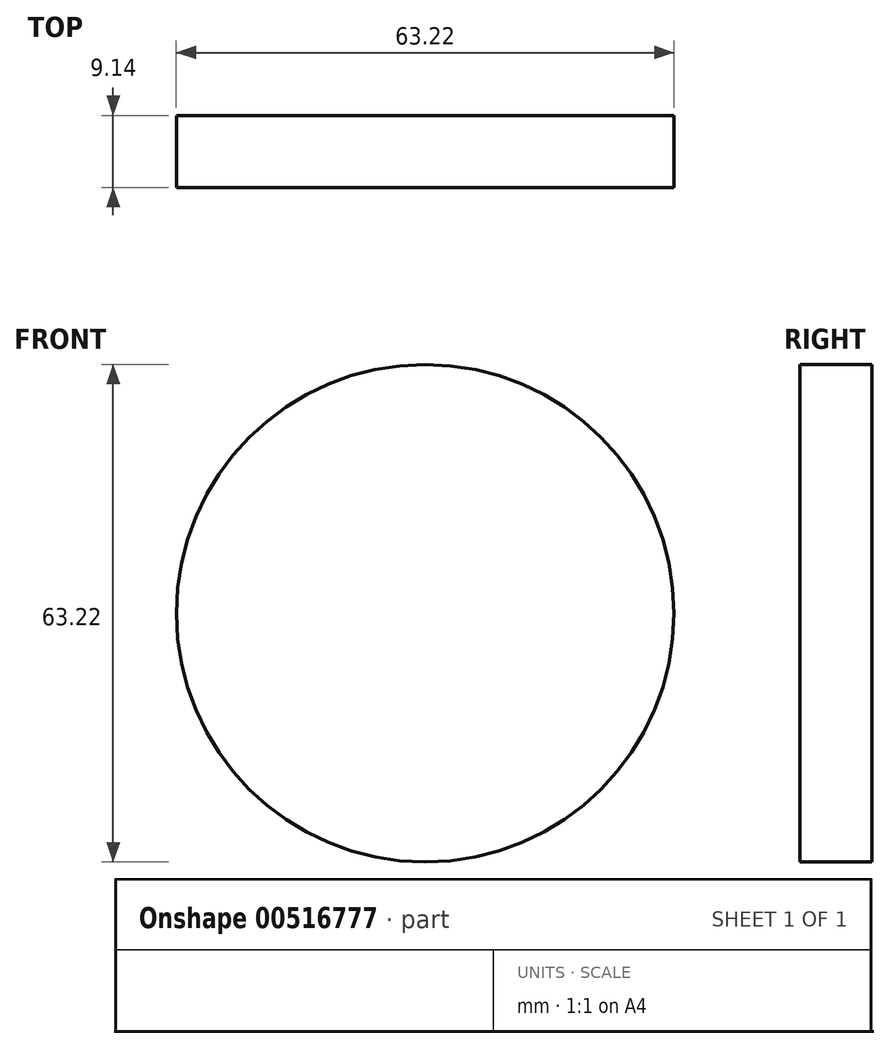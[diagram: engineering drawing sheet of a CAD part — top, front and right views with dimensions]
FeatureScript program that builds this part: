
annotation { "Feature Type Name" : "Feature", "Feature Type Description" : "" }
export const myFeature = defineFeature(function(context is Context, id is Id, definition is map)
    precondition{}
    {
        {
            var Q0;
            Q0=qCreatedBy(makeId("Front.planeOp"),FACE);
            var sketch = newSketch(context, id + "F0", { "sketchPlane" : qUnion([Q0])});
            skCircle(sketch, "E0", {"center": v(0, 0) * mm, "radius": 31.6 * mm});
            skSolve(sketch);
        }
        {
            var Q0;
            Q0=sQuery(id+"F0.wireOp",EDGE,"E0");
            extrude(context, id + "F1", {"bodyType" : ToolBodyType.SURFACE, "surfaceEntities" : qUnion([Q0]), "depth" : 9.14 * mm, "offsetDistance" : 25.4 * mm});
        }
    });
